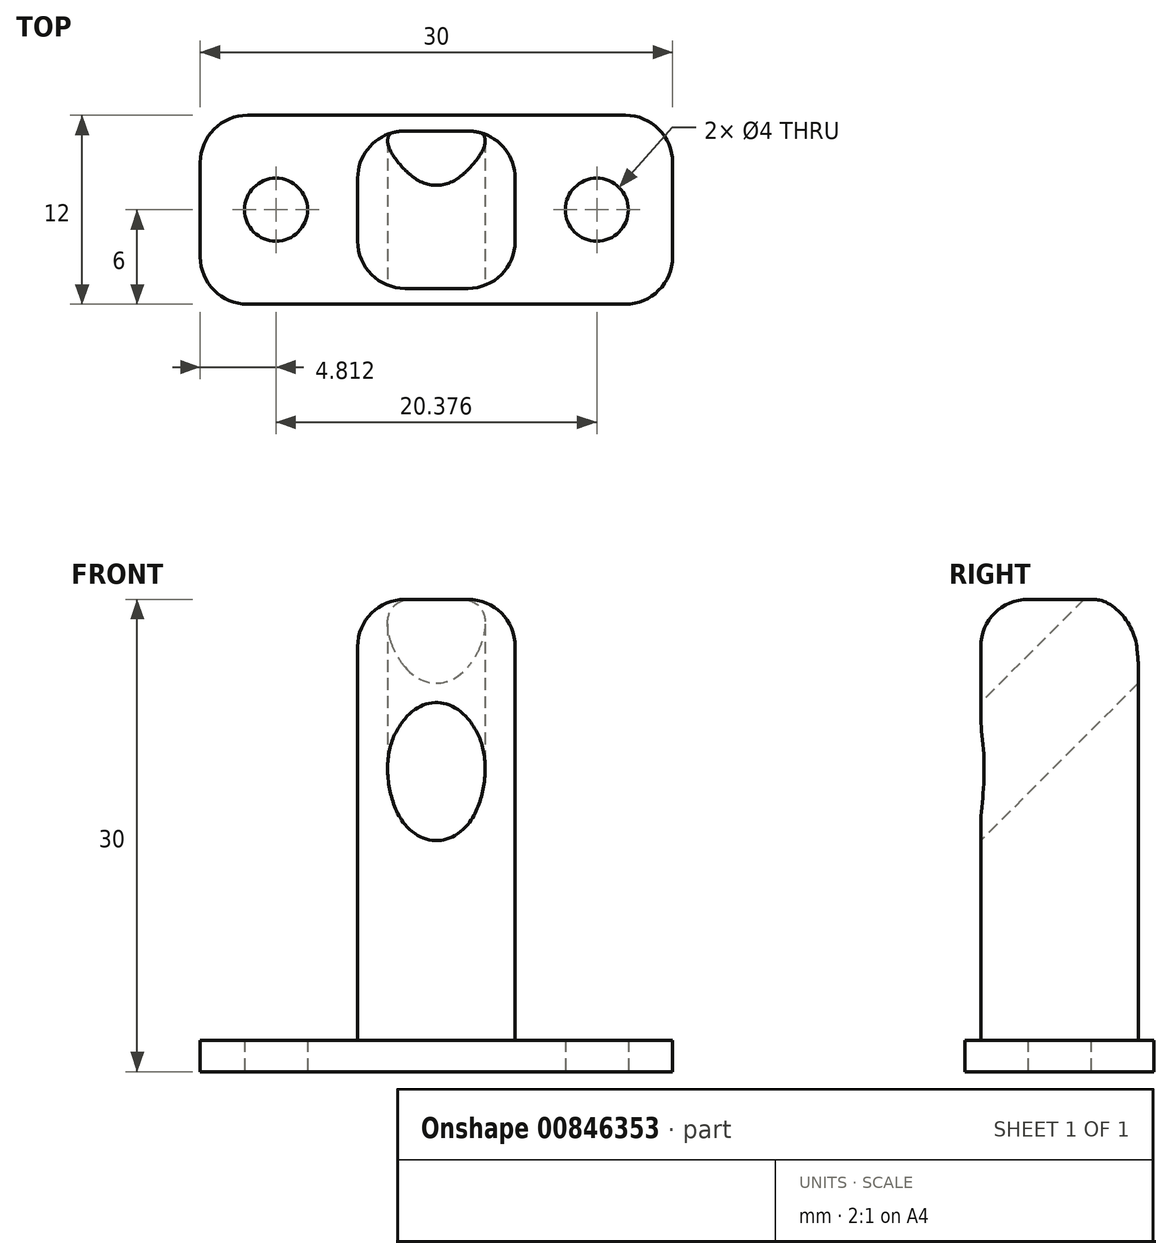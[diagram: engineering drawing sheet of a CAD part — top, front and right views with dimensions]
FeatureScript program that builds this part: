
annotation { "Feature Type Name" : "Feature", "Feature Type Description" : "" }
export const myFeature = defineFeature(function(context is Context, id is Id, definition is map)
    precondition{}
    {
        {
            var Q0;
            Q0=qCreatedBy(makeId("Top.planeOp"),FACE);
            var sketch = newSketch(context, id + "F0", { "sketchPlane" : qUnion([Q0])});
            skLineSegment(sketch, "E0.bottom", {"start": v(15, -6) * mm, "end": v(-15, -6) * mm});
            skLineSegment(sketch, "E0.top", {"start": v(15, 6) * mm, "end": v(-15, 6) * mm});
            skLineSegment(sketch, "E0.left", {"start": v(15, -6) * mm, "end": v(15, 6) * mm});
            skLineSegment(sketch, "E0.right", {"start": v(-15, -6) * mm, "end": v(-15, 6) * mm});
            skPoint(sketch, "E0.middle", {"position": v(0, 0) * mm});
            skLineSegment(sketch, "E1.bottom", {"start": v(5, -5) * mm, "end": v(-5, -5) * mm});
            skLineSegment(sketch, "E1.top", {"start": v(5, 5) * mm, "end": v(-5, 5) * mm});
            skLineSegment(sketch, "E1.left", {"start": v(5, -5) * mm, "end": v(5, 5) * mm});
            skLineSegment(sketch, "E1.right", {"start": v(-5, -5) * mm, "end": v(-5, 5) * mm});
            skCircle(sketch, "E2", {"center": v(-10.19, 0) * mm, "radius": 2 * mm});
            skCircle(sketch, "E3.MirrorC", {"center": v(10.19, 0) * mm, "radius": 2 * mm});
            skSolve(sketch);
        }
        {
            var Q0;
            Q0=makeQuery(id+"F0.imprint","IMPRINT",FACE,{"disambiguationData":[TD([[makeQuery(id+"F0.imprint","IMPRINT",EDGE,{"derivedFrom":sQuery(id+"F0.wireOp",EDGE,"E0.bottom")}),-1.0]])]});
            var Q1;
            Q1=makeQuery(id+"F0.imprint","IMPRINT",FACE,{"disambiguationData":[TD([[makeQuery(id+"F0.imprint","IMPRINT",EDGE,{"derivedFrom":sQuery(id+"F0.wireOp",EDGE,"E1.bottom")}),-1.0]])]});
            extrude(context, id + "F1", {"entities" : qUnion([Q0, Q1]), "depth" : 2 * mm, "offsetDistance" : 25 * mm});
        }
        {
            var Q0;
            Q0=makeQuery(id+"F0.imprint","IMPRINT",FACE,{"disambiguationData":[TD([[makeQuery(id+"F0.imprint","IMPRINT",EDGE,{"derivedFrom":sQuery(id+"F0.wireOp",EDGE,"E1.bottom")}),-1.0]])]});
            extrude(context, id + "F2", {"entities" : qUnion([Q0]), "operationType" : NewBodyOperationType.ADD, "depth" : 30 * mm, "offsetDistance" : 25 * mm});
        }
        {
            var Q0;
            Q0=makeQuery(id+"F1.opExtrude","SWEPT_EDGE",EDGE,{"disambiguationData":[OSD([sQuery(id+"F0.wireOp",EDGE,"E0.bottom"),sQuery(id+"F0.wireOp",EDGE,"E0.right")])]});
            var Q1;
            Q1=makeQuery(id+"F2.opExtrude","SWEPT_EDGE",EDGE,{"disambiguationData":[OSD([sQuery(id+"F0.wireOp",EDGE,"E1.bottom"),sQuery(id+"F0.wireOp",EDGE,"E1.right")])]});
            var Q2;
            Q2=makeQuery(id+"F2.opExtrude","SWEPT_EDGE",EDGE,{"disambiguationData":[OSD([sQuery(id+"F0.wireOp",EDGE,"E1.bottom"),sQuery(id+"F0.wireOp",EDGE,"E1.left")])]});
            var Q3;
            Q3=makeQuery(id+"F2.opExtrude","SWEPT_EDGE",EDGE,{"disambiguationData":[OSD([sQuery(id+"F0.wireOp",EDGE,"E1.top"),sQuery(id+"F0.wireOp",EDGE,"E1.left")])]});
            var Q4;
            Q4=makeQuery(id+"F1.opExtrude","SWEPT_EDGE",EDGE,{"disambiguationData":[OSD([sQuery(id+"F0.wireOp",EDGE,"E0.bottom"),sQuery(id+"F0.wireOp",EDGE,"E0.left")])]});
            var Q5;
            Q5=makeQuery(id+"F1.opExtrude","SWEPT_EDGE",EDGE,{"disambiguationData":[OSD([sQuery(id+"F0.wireOp",EDGE,"E0.top"),sQuery(id+"F0.wireOp",EDGE,"E0.left")])]});
            var Q6;
            Q6=makeQuery(id+"F2.opExtrude","SWEPT_EDGE",EDGE,{"disambiguationData":[OSD([sQuery(id+"F0.wireOp",EDGE,"E1.top"),sQuery(id+"F0.wireOp",EDGE,"E1.right")])]});
            var Q7;
            Q7=makeQuery(id+"F1.opExtrude","SWEPT_EDGE",EDGE,{"disambiguationData":[OSD([sQuery(id+"F0.wireOp",EDGE,"E0.top"),sQuery(id+"F0.wireOp",EDGE,"E0.right")])]});
            var Q8;
            Q8=makeQuery(id+"F2.opExtrude","CAP_EDGE",EDGE,{"disambiguationData":[OSD([sQuery(id+"F0.wireOp",EDGE,"E1.left")])],"isStart":false});
            var Q9;
            Q9=makeQuery(id+"F2.opExtrude","CAP_EDGE",EDGE,{"disambiguationData":[OSD([sQuery(id+"F0.wireOp",EDGE,"E1.top")])],"isStart":false});
            var Q10;
            Q10=makeQuery(id+"F2.opExtrude","CAP_EDGE",EDGE,{"disambiguationData":[OSD([sQuery(id+"F0.wireOp",EDGE,"E1.right")])],"isStart":false});
            var Q11;
            Q11=makeQuery(id+"F2.opExtrude","CAP_EDGE",EDGE,{"disambiguationData":[OSD([sQuery(id+"F0.wireOp",EDGE,"E1.bottom")])],"isStart":false});
            fillet(context, id + "F3", {"entities" : qUnion([Q0, Q1, Q2, Q3, Q4, Q5, Q6, Q7, Q8, Q9, Q10, Q11]), "radius" : 3 * mm, "tangentPropagation" : true, "allowEdgeOverflow" : false});
        }
        {
            var Q0;
            Q0=makeQuery(id+"F1.opExtrude","CAP_EDGE",EDGE,{"disambiguationData":[OSD([sQuery(id+"F0.wireOp",EDGE,"E0.bottom")])],"isStart":true});
            cPlane(context, id + "F4", {"entities" : qUnion([Q0]), "cplaneType" : CPlaneType.LINE_ANGLE, "offset" : 25 * mm, "angle" : 45 * degree, "oppositeDirection" : true, "width" : 150 * mm, "height" : 150 * mm});
        }
        {
            var Q0;
            Q0=qCreatedBy(id+"F4.planeOp",FACE);
            var sketch = newSketch(context, id + "F5", { "sketchPlane" : qUnion([Q0])});
            skCircle(sketch, "E4", {"center": v(0, 17.01) * mm, "radius": 3.1 * mm});
            skSolve(sketch);
        }
        {
            var Q0;
            Q0=makeQuery(id+"F5.imprint","IMPRINT",FACE,{"disambiguationData":[TD([[makeQuery(id+"F5.imprint","IMPRINT",EDGE,{"derivedFrom":sQuery(id+"F5.wireOp",EDGE,"E4")}),1.0]])]});
            extrude(context, id + "F6", {"entities" : qUnion([Q0]), "operationType" : NewBodyOperationType.REMOVE, "oppositeDirection" : true, "depth" : 100 * mm, "offsetDistance" : 25 * mm});
        }
    });
